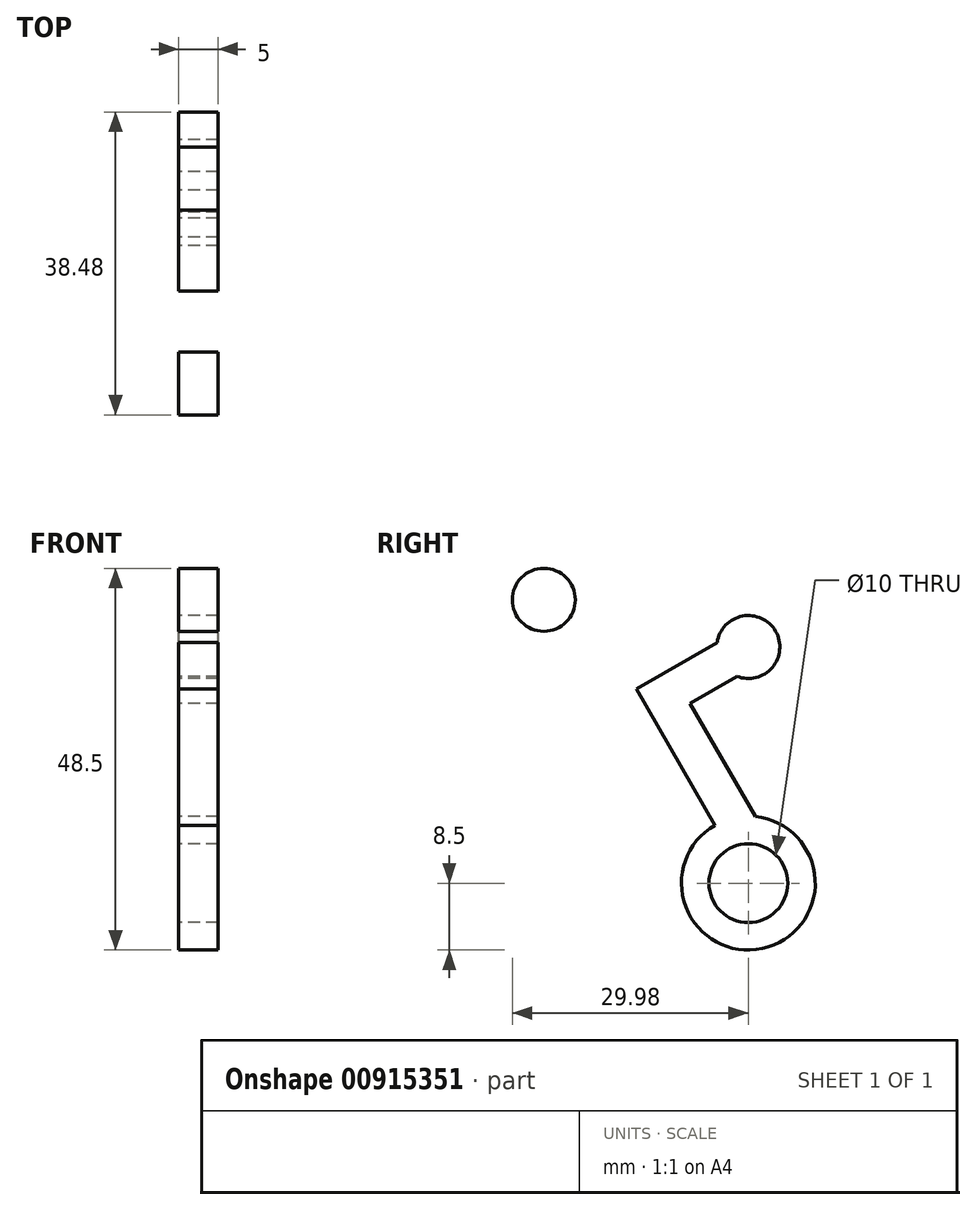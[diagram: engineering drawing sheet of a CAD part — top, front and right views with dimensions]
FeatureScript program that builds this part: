
annotation { "Feature Type Name" : "Feature", "Feature Type Description" : "" }
export const myFeature = defineFeature(function(context is Context, id is Id, definition is map)
    precondition{}
    {
        {
            var Q0;
            Q0=qCreatedBy(makeId("Right.planeOp"),FACE);
            var sketch = newSketch(context, id + "F0", { "sketchPlane" : qUnion([Q0])});
            skCircle(sketch, "E0", {"center": v(0, 0) * mm, "radius": 5 * mm});
            skArc(sketch, "E1", {"start": v(-4.25, 7.36) * mm, "mid": v(1.76, -8.31) * mm, "end": v(0.9, 8.45) * mm});
            skArc(sketch, "E2", {"start": v(-1.45, 26.27) * mm, "mid": v(3.46, 32) * mm, "end": v(-3.95, 30.6) * mm});
            skLineSegment(sketch, "E3", {"start": v(0, 0) * mm, "end": v(0, 30) * mm, "construction": true});
            skLineSegment(sketch, "E4", {"start": v(0, 0) * mm, "end": v(-25.98, 0) * mm, "construction": true});
            skCircle(sketch, "E5", {"center": v(-25.98, 36) * mm, "radius": 4 * mm});
            skLineSegment(sketch, "E6", {"start": v(-4.25, 7.36) * mm, "end": v(-14.24, 24.67) * mm});
            skLineSegment(sketch, "E7", {"start": v(0, 30) * mm, "end": v(-13, 22.5) * mm, "construction": true});
            skLineSegment(sketch, "E8", {"start": v(-14.24, 24.67) * mm, "end": v(-3.95, 30.6) * mm});
            skLineSegment(sketch, "E9", {"start": v(-1.45, 26.27) * mm, "end": v(-7.41, 22.83) * mm});
            skLineSegment(sketch, "E10", {"start": v(-7.41, 22.83) * mm, "end": v(0.9, 8.45) * mm});
            skCircle(sketch, "E11", {"center": v(-25.98, 15) * mm, "radius": 4 * mm, "construction": true});
            skLineSegment(sketch, "E12", {"start": v(0, 0) * mm, "end": v(-13, 22.5) * mm, "construction": true});
            skLineSegment(sketch, "E13", {"start": v(-25.98, 0) * mm, "end": v(-25.98, 15) * mm, "construction": true});
            skLineSegment(sketch, "E14", {"start": v(0, 0) * mm, "end": v(0, 25.98) * mm, "construction": true});
            skLineSegment(sketch, "E15", {"start": v(0, 25.98) * mm, "end": v(15, 25.98) * mm, "construction": true});
            skCircle(sketch, "E16", {"center": v(15, 25.98) * mm, "radius": 4 * mm, "construction": true});
            skLineSegment(sketch, "E17", {"start": v(19, 24.98) * mm, "end": v(19, 32) * mm});
            skLineSegment(sketch, "E18", {"start": v(-25.98, 32) * mm, "end": v(-25.98, 19) * mm, "construction": true});
            skLineSegment(sketch, "E19", {"start": v(47.72, 32) * mm, "end": v(47.72, 19) * mm, "construction": true});
            skSolve(sketch);
        }
        {
            var Q0;
            Q0 = qSketchRegion(id + "F0", true);
            extrude(context, id + "F1", {"entities" : qUnion([Q0]), "endBound" : BoundingType.SYMMETRIC, "depth" : 5 * mm, "offsetDistance" : 25 * mm});
        }
    });
